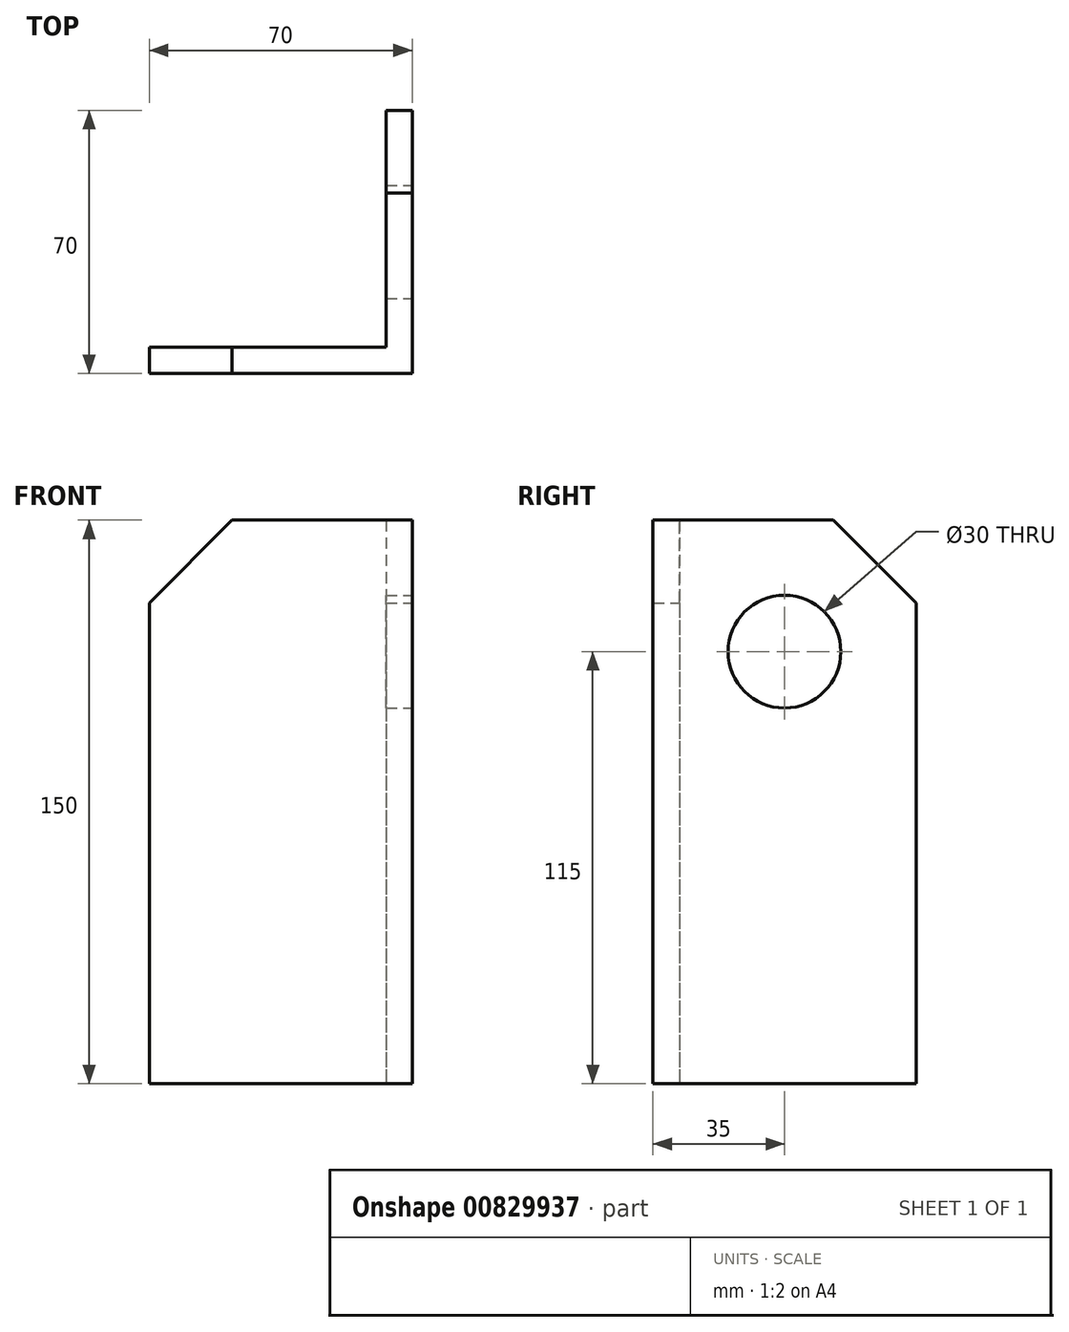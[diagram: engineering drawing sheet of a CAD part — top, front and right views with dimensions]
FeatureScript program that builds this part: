
annotation { "Feature Type Name" : "Feature", "Feature Type Description" : "" }
export const myFeature = defineFeature(function(context is Context, id is Id, definition is map)
    precondition{}
    {
        {
            var Q0;
            Q0=qCreatedBy(makeId("Top.planeOp"),FACE);
            var sketch = newSketch(context, id + "F0", { "sketchPlane" : qUnion([Q0])});
            skLineSegment(sketch, "E0", {"start": v(0, 0) * mm, "end": v(0, 70) * mm});
            skLineSegment(sketch, "E1", {"start": v(0, 0) * mm, "end": v(-70, 0) * mm});
            skLineSegment(sketch, "E2", {"start": v(0, 70) * mm, "end": v(-7, 70) * mm});
            skLineSegment(sketch, "E3", {"start": v(-7, 70) * mm, "end": v(-7, 7) * mm});
            skLineSegment(sketch, "E4", {"start": v(-7, 7) * mm, "end": v(-70, 7) * mm});
            skLineSegment(sketch, "E5", {"start": v(-70, 7) * mm, "end": v(-70, 0) * mm});
            skSolve(sketch);
        }
        {
            var Q0;
            Q0=makeQuery(id+"F0.imprint","IMPRINT",FACE,{"disambiguationData":[TD([[makeQuery(id+"F0.imprint","IMPRINT",EDGE,{"derivedFrom":sQuery(id+"F0.wireOp",EDGE,"E0")}),1.0]])]});
            extrude(context, id + "F1", {"entities" : qUnion([Q0]), "depth" : 150 * mm, "offsetDistance" : 25 * mm});
        }
        {
            var Q0;
            Q0=makeQuery(id+"F1.opExtrude","CAP_EDGE",EDGE,{"disambiguationData":[OSD([sQuery(id+"F0.wireOp",EDGE,"E5")])],"isStart":false});
            var Q1;
            Q1=makeQuery(id+"F1.opExtrude","CAP_EDGE",EDGE,{"disambiguationData":[OSD([sQuery(id+"F0.wireOp",EDGE,"E2")])],"isStart":false});
            chamfer(context, id + "F2", {"entities" : qUnion([Q0, Q1]), "width" : 22 * mm, "tangentPropagation" : true});
        }
        {
            var Q0;
            Q0=makeQuery(id+"F1.opExtrude","SWEPT_FACE",FACE,{"disambiguationData":[OSD([sQuery(id+"F0.wireOp",EDGE,"E0")])]});
            var sketch = newSketch(context, id + "F3", { "sketchPlane" : qUnion([Q0])});
            skCircle(sketch, "E6", {"center": v(35, 115) * mm, "radius": 15 * mm});
            skSolve(sketch);
        }
        {
            var Q0;
            Q0=makeQuery(id+"F3.imprint","IMPRINT",FACE,{"disambiguationData":[TD([[makeQuery(id+"F3.imprint","IMPRINT",EDGE,{"derivedFrom":sQuery(id+"F3.wireOp",EDGE,"E6")}),1.0]])]});
            extrude(context, id + "F4", {"entities" : qUnion([Q0]), "operationType" : NewBodyOperationType.REMOVE, "oppositeDirection" : true, "depth" : 25 * mm, "offsetDistance" : 25 * mm});
        }
    });
